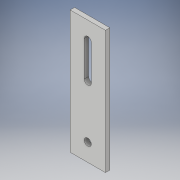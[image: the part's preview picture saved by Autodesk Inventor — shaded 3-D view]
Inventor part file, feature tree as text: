
AUTODESK INVENTOR PART (.ipt)
format: ipt  version: 2018 (Build 220112000, 112)  size: 104,448 bytes
history: native  units: in
note: dims shown in document units (in); Inventor stores cm internally (conversion verified against a paired STEP export)
features: extrude x1, sketch x1
ambient origin geometry x8: Origin, YZ Plane, XZ Plane, XY Plane, X Axis, Y Axis, Z Axis, Center Point
bodies: Body1 (feature_tree)
feature tree (2):
  extrude  "Extrusion2"  Depth=3.5in
  sketch  "Sketch1"  dims[d0=1.0in d1=3.5in d2=0.5in d3=0.5in d7=1.0in d8=0.125in d9=0.0in]
